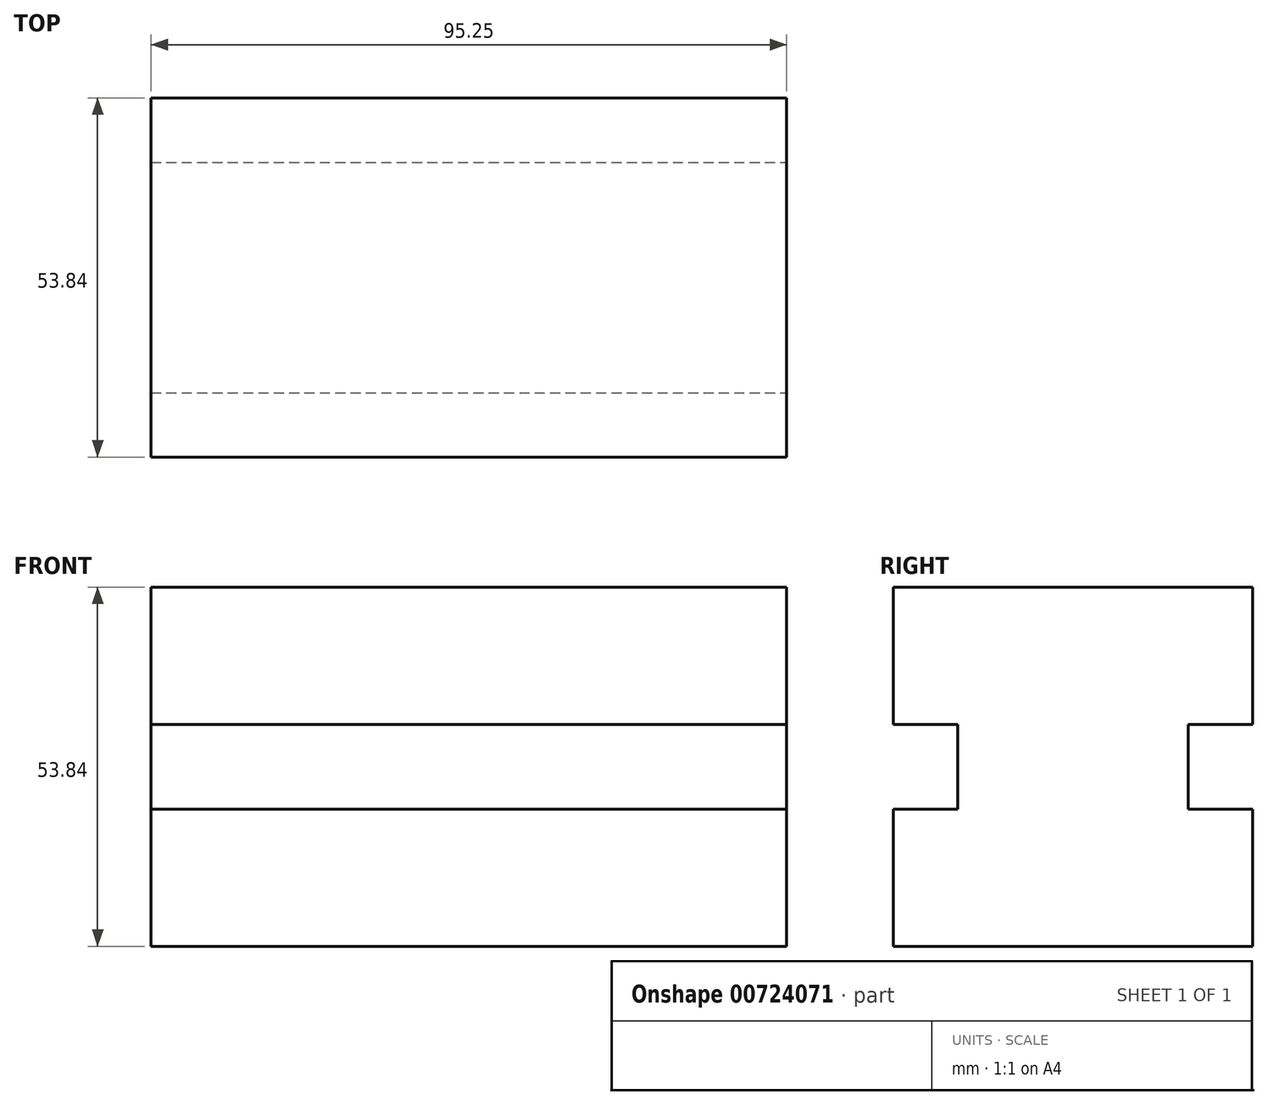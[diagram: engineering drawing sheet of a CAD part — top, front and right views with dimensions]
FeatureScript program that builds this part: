
annotation { "Feature Type Name" : "Feature", "Feature Type Description" : "" }
export const myFeature = defineFeature(function(context is Context, id is Id, definition is map)
    precondition{}
    {
        {
            var Q0;
            Q0=qCreatedBy(makeId("Right.planeOp"),FACE);
            var sketch = newSketch(context, id + "F0", { "sketchPlane" : qUnion([Q0])});
            skLineSegment(sketch, "E0.bottom", {"start": v(26.92, -26.92) * mm, "end": v(-26.92, -26.92) * mm});
            skLineSegment(sketch, "E0.top", {"start": v(26.92, 26.92) * mm, "end": v(-26.92, 26.92) * mm});
            skLineSegment(sketch, "E0.left", {"start": v(26.92, -26.92) * mm, "end": v(26.92, -6.35) * mm});
            skLineSegment(sketch, "E0.right", {"start": v(-26.92, -26.92) * mm, "end": v(-26.92, -6.35) * mm});
            skPoint(sketch, "E0.middle", {"position": v(0, 0) * mm});
            skLineSegment(sketch, "E1.left", {"start": v(-26.92, 12.7) * mm, "end": v(-26.92, 6.35) * mm});
            skLineSegment(sketch, "E2", {"start": v(-26.92, 6.35) * mm, "end": v(-17.27, 6.35) * mm});
            skLineSegment(sketch, "E3", {"start": v(-17.27, 6.35) * mm, "end": v(-17.27, -6.35) * mm});
            skLineSegment(sketch, "E4", {"start": v(-17.27, -6.35) * mm, "end": v(-26.92, -6.35) * mm});
            skLineSegment(sketch, "E5.trimOffspring", {"start": v(-26.92, 6.35) * mm, "end": v(-26.92, 26.92) * mm});
            skLineSegment(sketch, "E6", {"start": v(0, 34.53) * mm, "end": v(0, -38.4) * mm, "construction": true});
            skLineSegment(sketch, "E7.MirrorCS", {"start": v(26.92, 6.35) * mm, "end": v(17.27, 6.35) * mm});
            skLineSegment(sketch, "E8.MirrorCS", {"start": v(17.27, 6.35) * mm, "end": v(17.27, -6.35) * mm});
            skLineSegment(sketch, "E9.MirrorCS", {"start": v(17.27, -6.35) * mm, "end": v(26.92, -6.35) * mm});
            skLineSegment(sketch, "E10.trimOffspring", {"start": v(26.92, 6.35) * mm, "end": v(26.92, 26.92) * mm});
            skSolve(sketch);
        }
        {
            var Q0;
            Q0=makeQuery(id+"F0.imprint","IMPRINT",FACE,{"disambiguationData":[TD([[makeQuery(id+"F0.imprint","IMPRINT",EDGE,{"derivedFrom":sQuery(id+"F0.wireOp",EDGE,"E0.bottom")}),-1.0]])]});
            extrude(context, id + "F1", {"entities" : qUnion([Q0]), "oppositeDirection" : true, "depth" : 95.25 * mm, "offsetDistance" : 25.4 * mm});
        }
    });
